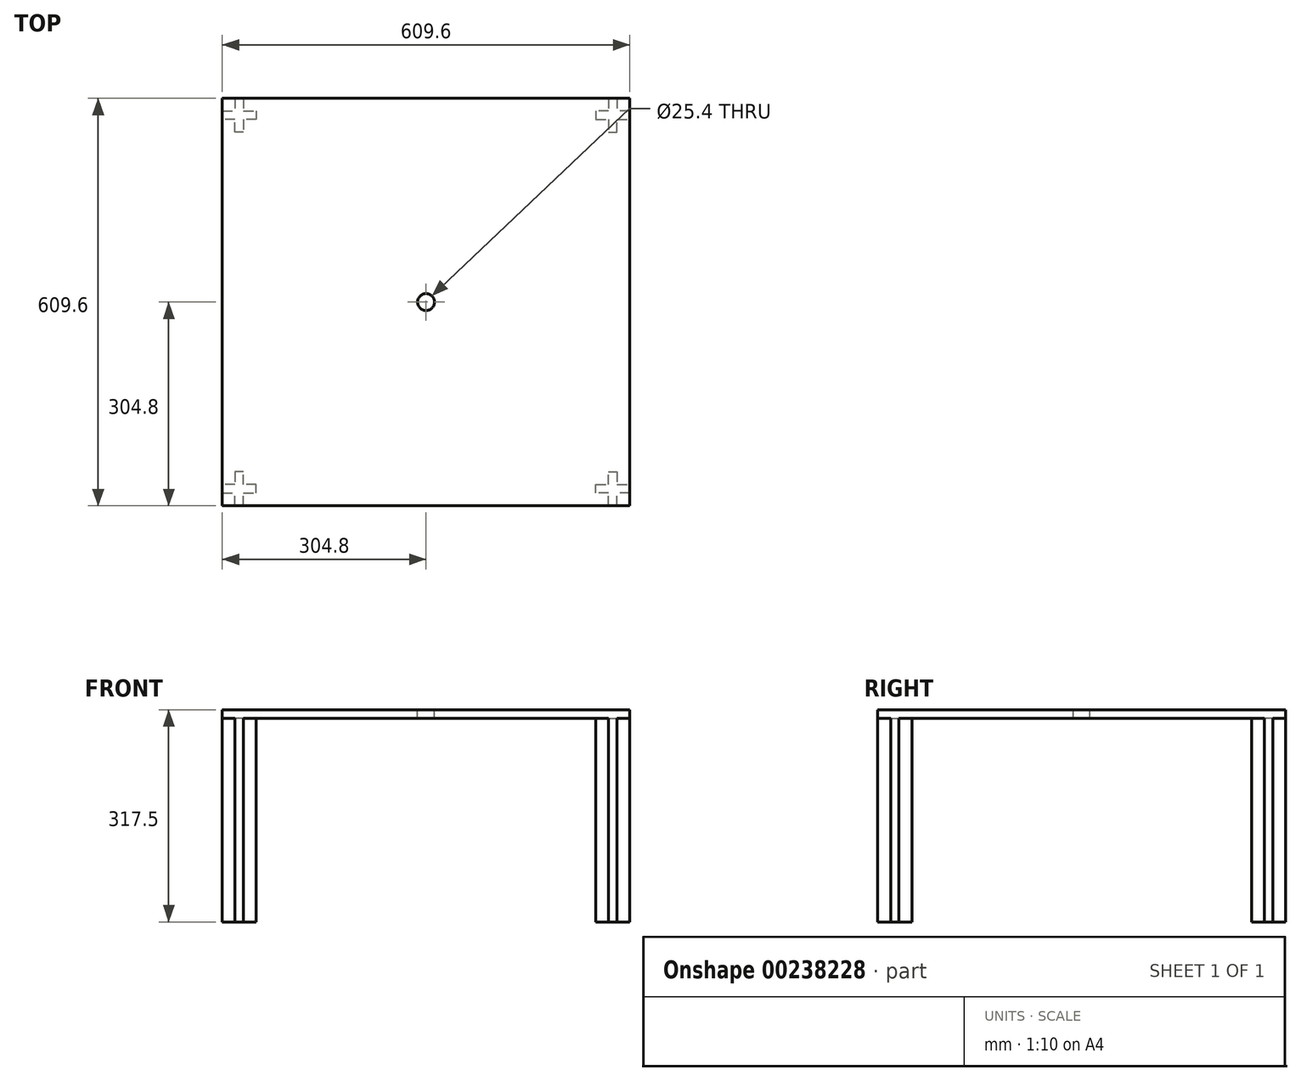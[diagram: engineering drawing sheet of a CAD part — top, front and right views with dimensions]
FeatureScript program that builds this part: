
annotation { "Feature Type Name" : "Feature", "Feature Type Description" : "" }
export const myFeature = defineFeature(function(context is Context, id is Id, definition is map)
    precondition{}
    {
        {
            var Q0;
            Q0=qCreatedBy(makeId("Top.planeOp"),FACE);
            var sketch = newSketch(context, id + "F0", { "sketchPlane" : qUnion([Q0])});
            skLineSegment(sketch, "E0.bottom", {"start": v(0, 0) * mm, "end": v(609.6, 0) * mm});
            skLineSegment(sketch, "E0.top", {"start": v(0, 609.6) * mm, "end": v(609.6, 609.6) * mm});
            skLineSegment(sketch, "E0.left", {"start": v(0, 0) * mm, "end": v(0, 609.6) * mm});
            skLineSegment(sketch, "E0.right", {"start": v(609.6, 0) * mm, "end": v(609.6, 609.6) * mm});
            skSolve(sketch);
        }
        {
            var Q0;
            Q0=makeQuery(id+"F0.imprint","IMPRINT",FACE,{"disambiguationData":[TD([[makeQuery(id+"F0.imprint","IMPRINT",EDGE,{"derivedFrom":sQuery(id+"F0.wireOp",EDGE,"E0.bottom")}),1.0]])]});
            extrude(context, id + "F1", {"entities" : qUnion([Q0]), "endBound" : BoundingType.SYMMETRIC, "depth" : 12.7 * mm});
        }
        {
            var Q0;
            Q0=makeQuery(id+"F1.opExtrude","CAP_FACE",FACE,{"disambiguationData":[OSD([sQuery(id+"F0.wireOp",EDGE,"E0.bottom"),sQuery(id+"F0.wireOp",EDGE,"E0.top"),sQuery(id+"F0.wireOp",EDGE,"E0.left"),sQuery(id+"F0.wireOp",EDGE,"E0.right")])],"isStart":true});
            var sketch = newSketch(context, id + "F2", { "sketchPlane" : qUnion([Q0])});
            skLineSegment(sketch, "E1", {"start": v(304.8, 0) * mm, "end": v(304.8, -609.6) * mm, "construction": true});
            skLineSegment(sketch, "E2", {"start": v(609.6, -304.8) * mm, "end": v(0, -304.8) * mm, "construction": true});
            skLineSegment(sketch, "E3.top", {"start": v(0, -19.05) * mm, "end": v(19.05, -19.05) * mm});
            skLineSegment(sketch, "E3.right", {"start": v(19.05, 0) * mm, "end": v(19.05, -19.05) * mm});
            skLineSegment(sketch, "E4", {"start": v(19.05, 0) * mm, "end": v(31.75, 0) * mm});
            skLineSegment(sketch, "E5", {"start": v(31.75, 0) * mm, "end": v(31.75, -19.05) * mm});
            skLineSegment(sketch, "E6", {"start": v(31.75, -19.05) * mm, "end": v(50.8, -19.05) * mm});
            skLineSegment(sketch, "E7", {"start": v(50.8, -19.05) * mm, "end": v(50.8, -31.75) * mm});
            skLineSegment(sketch, "E8", {"start": v(50.8, -31.75) * mm, "end": v(31.75, -31.75) * mm});
            skLineSegment(sketch, "E9", {"start": v(31.75, -31.75) * mm, "end": v(31.75, -50.8) * mm});
            skLineSegment(sketch, "E10", {"start": v(31.75, -50.8) * mm, "end": v(19.05, -50.8) * mm});
            skLineSegment(sketch, "E11", {"start": v(19.05, -50.8) * mm, "end": v(19.05, -31.75) * mm});
            skLineSegment(sketch, "E12", {"start": v(19.05, -31.75) * mm, "end": v(0, -31.75) * mm});
            skLineSegment(sketch, "E13", {"start": v(0, -31.75) * mm, "end": v(0, -19.05) * mm});
            skLineSegment(sketch, "E14.MirrorCS", {"start": v(590.55, -31.75) * mm, "end": v(609.6, -31.75) * mm});
            skLineSegment(sketch, "E15.MirrorCS", {"start": v(590.55, -50.8) * mm, "end": v(590.55, -31.75) * mm});
            skLineSegment(sketch, "E16.MirrorCS", {"start": v(558.8, -19.05) * mm, "end": v(558.8, -31.75) * mm});
            skLineSegment(sketch, "E17.MirrorCS", {"start": v(577.85, -31.75) * mm, "end": v(577.85, -50.8) * mm});
            skLineSegment(sketch, "E18.MirrorCS", {"start": v(577.85, -19.05) * mm, "end": v(558.8, -19.05) * mm});
            skLineSegment(sketch, "E19.MirrorCS", {"start": v(558.8, -31.75) * mm, "end": v(577.85, -31.75) * mm});
            skLineSegment(sketch, "E20.MirrorCS", {"start": v(590.55, 0) * mm, "end": v(577.85, 0) * mm});
            skLineSegment(sketch, "E21.MirrorCS", {"start": v(577.85, -50.8) * mm, "end": v(590.55, -50.8) * mm});
            skLineSegment(sketch, "E22.MirrorCS", {"start": v(590.55, 0) * mm, "end": v(590.55, -19.05) * mm});
            skLineSegment(sketch, "E23.MirrorCS", {"start": v(609.6, -31.75) * mm, "end": v(609.6, -19.05) * mm});
            skLineSegment(sketch, "E24.MirrorCS", {"start": v(609.6, -19.05) * mm, "end": v(590.55, -19.05) * mm});
            skLineSegment(sketch, "E25.MirrorCS", {"start": v(577.85, 0) * mm, "end": v(577.85, -19.05) * mm});
            skLineSegment(sketch, "E26.MirrorCS", {"start": v(19.05, -609.6) * mm, "end": v(31.75, -609.6) * mm});
            skLineSegment(sketch, "E27.MirrorCS", {"start": v(590.55, -609.6) * mm, "end": v(577.85, -609.6) * mm});
            skLineSegment(sketch, "E28.MirrorCS", {"start": v(558.8, -590.55) * mm, "end": v(558.8, -577.85) * mm});
            skLineSegment(sketch, "E29.MirrorCS", {"start": v(0, -577.85) * mm, "end": v(0, -590.55) * mm});
            skLineSegment(sketch, "E30.MirrorCS", {"start": v(577.85, -558.8) * mm, "end": v(590.55, -558.8) * mm});
            skLineSegment(sketch, "E31.MirrorCS", {"start": v(31.75, -558.8) * mm, "end": v(19.05, -558.8) * mm});
            skLineSegment(sketch, "E32.MirrorCS", {"start": v(50.8, -590.55) * mm, "end": v(50.8, -577.85) * mm});
            skLineSegment(sketch, "E33.MirrorCS", {"start": v(609.6, -577.85) * mm, "end": v(609.6, -590.55) * mm});
            skLineSegment(sketch, "E34.MirrorCS", {"start": v(31.75, -590.55) * mm, "end": v(50.8, -590.55) * mm});
            skLineSegment(sketch, "E35.MirrorCS", {"start": v(31.75, -609.6) * mm, "end": v(31.75, -590.55) * mm});
            skLineSegment(sketch, "E36.MirrorCS", {"start": v(19.05, -609.6) * mm, "end": v(19.05, -590.55) * mm});
            skLineSegment(sketch, "E37.MirrorCS", {"start": v(0, -590.55) * mm, "end": v(19.05, -590.55) * mm});
            skLineSegment(sketch, "E38.MirrorCS", {"start": v(590.55, -558.8) * mm, "end": v(590.55, -577.85) * mm});
            skLineSegment(sketch, "E39.MirrorCS", {"start": v(590.55, -577.85) * mm, "end": v(609.6, -577.85) * mm});
            skLineSegment(sketch, "E40.MirrorCS", {"start": v(19.05, -558.8) * mm, "end": v(19.05, -577.85) * mm});
            skLineSegment(sketch, "E41.MirrorCS", {"start": v(577.85, -577.85) * mm, "end": v(577.85, -558.8) * mm});
            skLineSegment(sketch, "E42.MirrorCS", {"start": v(590.55, -609.6) * mm, "end": v(590.55, -590.55) * mm});
            skLineSegment(sketch, "E43.MirrorCS", {"start": v(577.85, -590.55) * mm, "end": v(558.8, -590.55) * mm});
            skLineSegment(sketch, "E44.MirrorCS", {"start": v(577.85, -609.6) * mm, "end": v(577.85, -590.55) * mm});
            skLineSegment(sketch, "E45.MirrorCS", {"start": v(609.6, -590.55) * mm, "end": v(590.55, -590.55) * mm});
            skLineSegment(sketch, "E46.MirrorCS", {"start": v(19.05, -577.85) * mm, "end": v(0, -577.85) * mm});
            skLineSegment(sketch, "E47.MirrorCS", {"start": v(31.75, -577.85) * mm, "end": v(31.75, -558.8) * mm});
            skLineSegment(sketch, "E48.MirrorCS", {"start": v(50.8, -577.85) * mm, "end": v(31.75, -577.85) * mm});
            skLineSegment(sketch, "E49.MirrorCS", {"start": v(558.8, -577.85) * mm, "end": v(577.85, -577.85) * mm});
            skSolve(sketch);
        }
        {
            var Q0;
            Q0=qSketchRegion(id+"F2",true);
            extrude(context, id + "F3", {"entities" : qUnion([Q0]), "operationType" : NewBodyOperationType.ADD, "depth" : 304.8 * mm});
        }
        {
            var Q0;
            Q0=makeQuery(id+"F1.opExtrude","CAP_FACE",FACE,{"disambiguationData":[OSD([sQuery(id+"F0.wireOp",EDGE,"E0.bottom"),sQuery(id+"F0.wireOp",EDGE,"E0.top"),sQuery(id+"F0.wireOp",EDGE,"E0.left"),sQuery(id+"F0.wireOp",EDGE,"E0.right")])],"isStart":false});
            var sketch = newSketch(context, id + "F4", { "sketchPlane" : qUnion([Q0])});
            skLineSegment(sketch, "E50", {"start": v(304.8, 609.6) * mm, "end": v(304.8, 304.8) * mm, "construction": true});
            skLineSegment(sketch, "E51", {"start": v(304.8, 304.8) * mm, "end": v(0, 304.8) * mm, "construction": true});
            skPoint(sketch, "E52.orphan", {"position": v(609.6, 304.8) * mm});
            skPoint(sketch, "E53.orphan", {"position": v(304.8, 0) * mm});
            skCircle(sketch, "E54", {"center": v(304.8, 304.8) * mm, "radius": 12.7 * mm});
            skSolve(sketch);
        }
        {
            var Q0;
            Q0=makeQuery(id+"F4.imprint","IMPRINT",FACE,{"disambiguationData":[TD([[makeQuery(id+"F4.imprint","IMPRINT",EDGE,{"derivedFrom":sQuery(id+"F4.wireOp",EDGE,"E54")}),1.0]])]});
            extrude(context, id + "F5", {"entities" : qUnion([Q0]), "operationType" : NewBodyOperationType.REMOVE, "endBound" : BoundingType.THROUGH_ALL, "oppositeDirection" : true, "depth" : 25.4 * mm});
        }
    });
